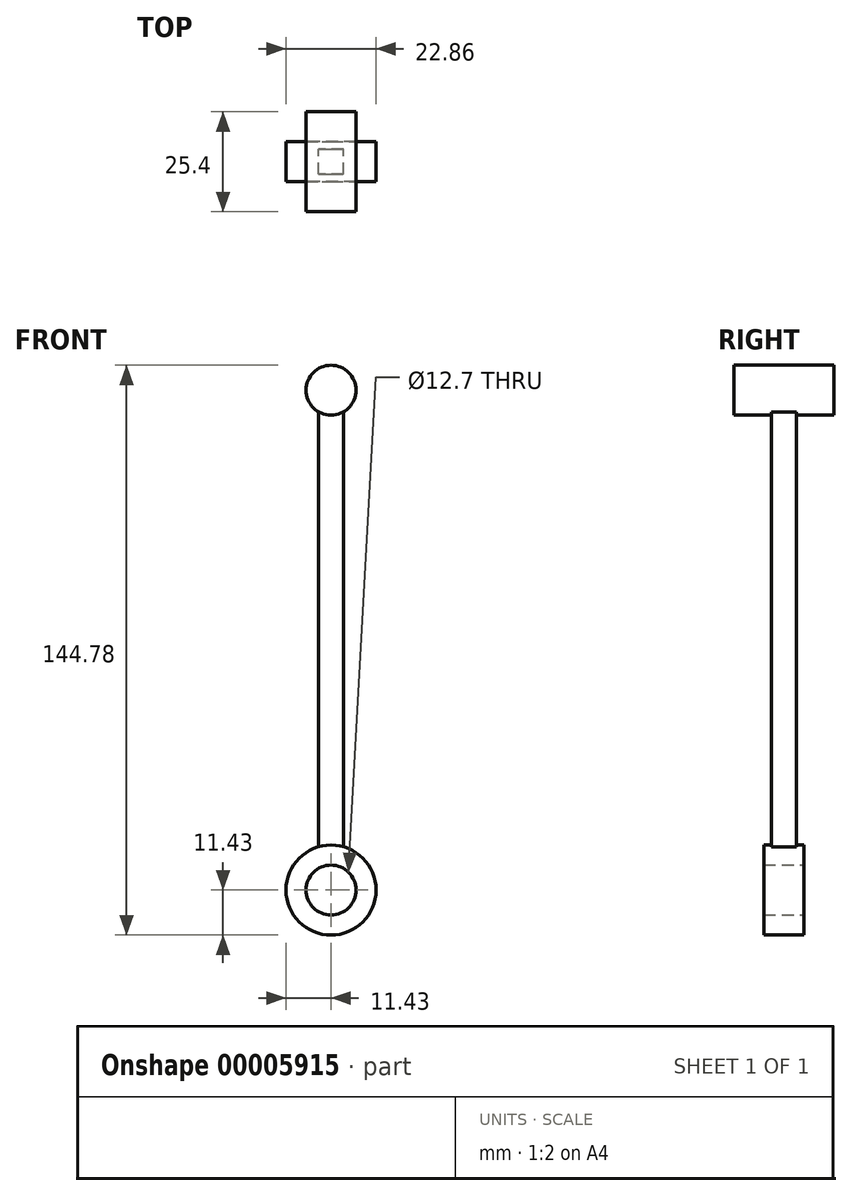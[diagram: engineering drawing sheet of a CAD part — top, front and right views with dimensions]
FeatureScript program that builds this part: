
annotation { "Feature Type Name" : "Feature", "Feature Type Description" : "" }
export const myFeature = defineFeature(function(context is Context, id is Id, definition is map)
    precondition{}
    {
        {
            var Q0;
            Q0=qCreatedBy(makeId("Front.planeOp"),FACE);
            var sketch = newSketch(context, id + "F0", { "sketchPlane" : qUnion([Q0])});
            skCircle(sketch, "E0", {"center": v(0, 0) * mm, "radius": 6.35 * mm});
            skCircle(sketch, "E1.0", {"center": v(0, 0) * mm, "radius": 11.43 * mm});
            skLineSegment(sketch, "E2", {"start": v(0, 0) * mm, "end": v(0, 127) * mm, "construction": true});
            skLineSegment(sketch, "E3.0", {"start": v(3.18, 10.98) * mm, "end": v(3.18, 121.5) * mm});
            skLineSegment(sketch, "E4.0", {"start": v(-3.18, 10.98) * mm, "end": v(-3.18, 121.5) * mm});
            skCircle(sketch, "E5", {"center": v(0, 127) * mm, "radius": 6.35 * mm});
            skSolve(sketch);
        }
        {
            var Q0;
            {var subQ2=sQuery(id+"F0.wireOp",EDGE,"E3.0");Q0=makeQuery(id+"F0.imprint","IMPRINT",FACE,{"disambiguationData":[TD([[makeQuery(id+"F0.imprint","IMPRINT",EDGE,{"derivedFrom":subQ2}),1.0]])]});}
            var Q1;
            Q1=sQuery(id+"F0.wireOp",EDGE,"E1.0");
            extrude(context, id + "F1", {"entities" : qUnion([Q0]), "surfaceEntities" : qUnion([Q1]), "endBound" : BoundingType.SYMMETRIC, "depth" : 6.35 * mm});
        }
        {
            var Q0;
            Q0=makeQuery(id+"F0.imprint","IMPRINT",FACE,{"disambiguationData":[TD([[makeQuery(id+"F0.imprint","IMPRINT",EDGE,{"derivedFrom":sQuery(id+"F0.wireOp",EDGE,"E0")}),-1.0]])]});
            extrude(context, id + "F2", {"entities" : qUnion([Q0]), "operationType" : NewBodyOperationType.ADD, "endBound" : BoundingType.SYMMETRIC, "depth" : 10.16 * mm});
        }
        {
            var Q0;
            {var subQ0=sQuery(id+"F0.wireOp",EDGE,"E5");var subQ2=makeQuery(id+"F0.imprint","INTERSECT",VERTEX,{"derivedFrom":[sQuery(id+"F0.wireOp",EDGE,"E3.0"),subQ0]});Q0=makeQuery(id+"F0.imprint","IMPRINT",FACE,{"disambiguationData":[TD([[makeQuery(id+"F0.imprint","IMPRINT",EDGE,{"disambiguationData":[TD([[subQ2,1.0]])],"derivedFrom":subQ0}),1.0]])]});}
            extrude(context, id + "F3", {"entities" : qUnion([Q0]), "operationType" : NewBodyOperationType.ADD, "endBound" : BoundingType.SYMMETRIC, "depth" : 25.4 * mm});
        }
    });
